# Revit family: CLighting-Luminii-Vesta_1_Direct-Indirect
name_source: partatom
category: Lighting Fixtures
units: mm (PartAtom-declared; Revit-internal decimal feet)

## family parameters
Cut with Voids When Loaded = No
Host = Face
Light Source = Yes
OmniClass Number = 23.80.70.11.14.17
OmniClass Title = Direct/Indirect
Part Type = Normal
Room Calculation Point = No
Round Connector Dimension = Use Diameter
Shared = Yes

## types (3) — shared parameters
Assembly Code = D5020230
CCT = 3500K
Canopy Finish = Metal - Luminii - Silver Anodized Aluminum
Color Filter = 16777215
Control Type = Consult Manufacturer Website for more Information
Control Zone = Consult Manufacturer Website for more Information
Current Amps = 50 A
Default Elevation = 0"
Depth = 4 15/16"
Description = Suspended linear system
Dimming Lamp Color Temperature Shift = <None>
Dimming Type = Consult Manufacturer Website for more Information
Emit Shape Visible in Rendering = No
Emit from Rectangle Length = 2 9/16"
Environment = Indoor
Finish = Metal - Luminii - Silver Anodized Aluminum
Frequency = 60 Hz
Has Battery Backup = No
Has Dimming = Yes
Housing Protection Rating = Consult Manufacturer Website for more Information
Initial Color Comments = Perfomance based on 3500K Photometric Web File
Keynote = 26 50 00
Lamp = LED
Lamp Life = 1
Lens Material = Plastic - Luminii - Frosted Lens
Load Classification = Lighting
Luminaire Type = Pendant Linear LED system
Manufacturer = Luminii
Model = Consult Manufacturer Website for more Information
Mounting Method = Ceiling Mount
Number of Poles = 1
Operating Temperature = Consult Manufacturer Website for more Information
Phase = 1
Power Factor = 1
Power Source Type = Driver
Product Page URL = https://www.luminii.com
Tilt Angle = 90.00°
URL = https://www.luminii.com
Version = 2020 - v1.0a
Voltage = 120 V
Voltage Comments = 120V | 277V | 347V
Warranty URL = https://www.luminii.com
Width = 2 9/16"

## per-type parameters (varying)
| type | Apparent Load | C Length Mid | Constraints | Emit from Rectangle Width | Length | Photometric Web File | Wattage Comments |
| 45.5" (B) | 4 VA | 22 3/4" | 2 | 45 1/2" | 45 1/2" | 356-90-4-35-FB-XX-04-04.IES | Direct (3.8W) - Indirect (3.9W) |
| 68" (C) | 6 VA | 34" | 3 | 68" | 68" | 356-90-4-35-FB-XX-04-06.IES | Direct (5.7W) - Indirect (5.6W) |
| 90.5" (D) | 9 VA | 45 1/4" | 4 | 90 1/2" | 90 1/2" | 356-90-4-35-FB-XX-04-08.IES | Direct (9.4W) - Indirect (7.4W) |

## geometry (parser evidence)
native form markers: Sweep x10
no freeform markers — native parametric forms only
